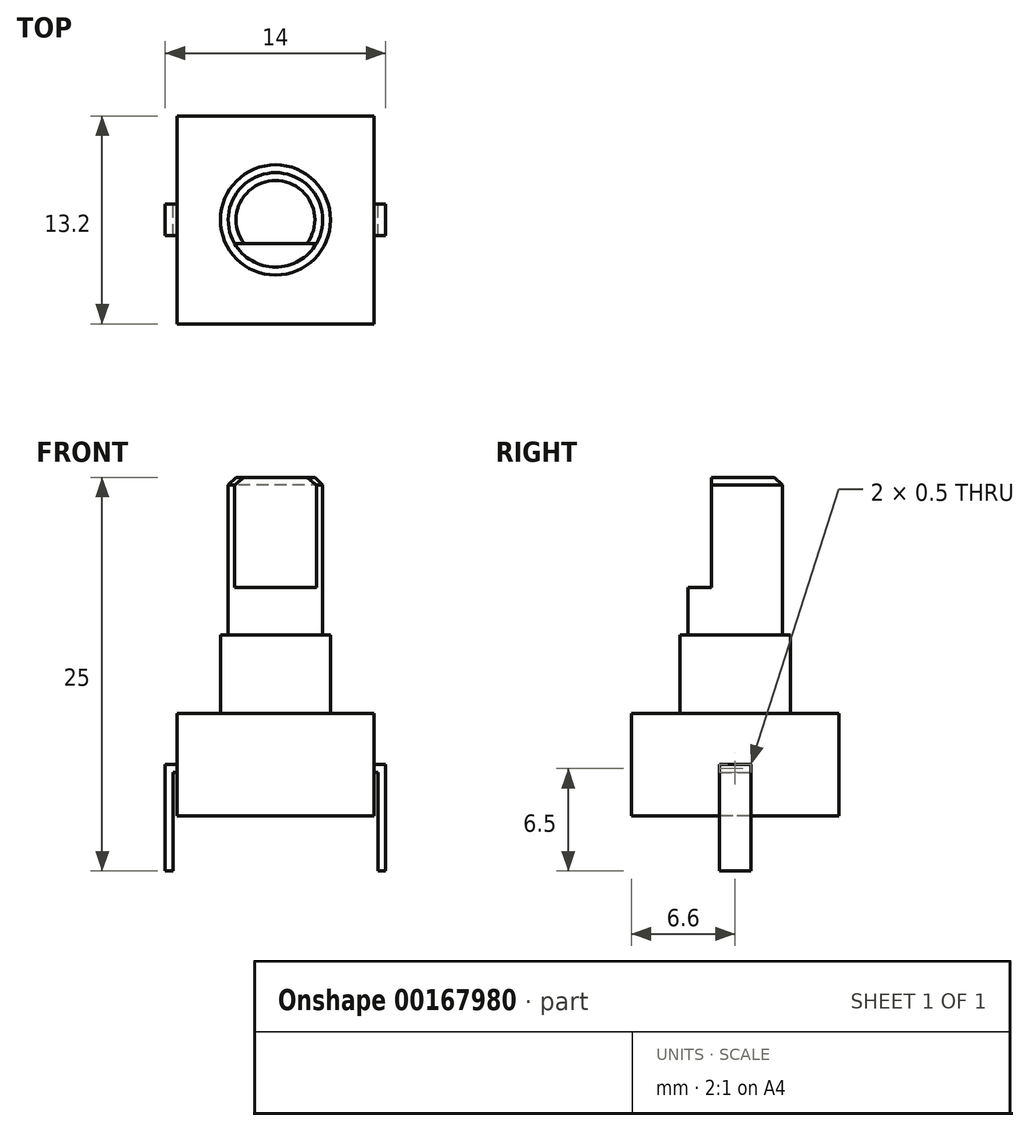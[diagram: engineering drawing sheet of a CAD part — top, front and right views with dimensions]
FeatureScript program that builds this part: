
annotation { "Feature Type Name" : "Feature", "Feature Type Description" : "" }
export const myFeature = defineFeature(function(context is Context, id is Id, definition is map)
    precondition{}
    {
        {
            var Q0;
            Q0=qCreatedBy(makeId("Top.planeOp"),FACE);
            var sketch = newSketch(context, id + "F0", { "sketchPlane" : qUnion([Q0])});
            skLineSegment(sketch, "E0.bottom", {"start": v(6.25, 6.6) * mm, "end": v(-6.25, 6.6) * mm});
            skLineSegment(sketch, "E0.top", {"start": v(6.25, -6.6) * mm, "end": v(-6.25, -6.6) * mm});
            skLineSegment(sketch, "E0.left", {"start": v(6.25, 6.6) * mm, "end": v(6.25, -6.6) * mm});
            skLineSegment(sketch, "E0.right", {"start": v(-6.25, 6.6) * mm, "end": v(-6.25, -6.6) * mm});
            skPoint(sketch, "E0.middle", {"position": v(0, 0) * mm});
            skSolve(sketch);
        }
        {
            var Q0;
            Q0 = qSketchRegion(id + "F0", true);
            extrude(context, id + "F1", {"entities" : qUnion([Q0]), "depth" : 6.5 * mm});
        }
        {
            var Q0;
            Q0=makeQuery(id+"F1.opExtrude","CAP_FACE",FACE,{"disambiguationData":[OSD([sQuery(id+"F0.wireOp",EDGE,"E0.bottom"),sQuery(id+"F0.wireOp",EDGE,"E0.top"),sQuery(id+"F0.wireOp",EDGE,"E0.left"),sQuery(id+"F0.wireOp",EDGE,"E0.right")])],"isStart":false});
            var sketch = newSketch(context, id + "F2", { "sketchPlane" : qUnion([Q0])});
            skCircle(sketch, "E1", {"center": v(0, 0) * mm, "radius": 3.5 * mm});
            skSolve(sketch);
        }
        {
            var Q0;
            Q0 = qSketchRegion(id + "F2", true);
            extrude(context, id + "F3", {"entities" : qUnion([Q0]), "operationType" : NewBodyOperationType.ADD, "depth" : 5 * mm});
        }
        {
            var Q0;
            Q0=makeQuery(id+"F3.opExtrude","CAP_FACE",FACE,{"disambiguationData":[OSD([sQuery(id+"F2.wireOp",EDGE,"E1")])],"isStart":false});
            var sketch = newSketch(context, id + "F4", { "sketchPlane" : qUnion([Q0])});
            skCircle(sketch, "E2", {"center": v(0, 0) * mm, "radius": 3 * mm});
            skSolve(sketch);
        }
        {
            var Q0;
            Q0 = qSketchRegion(id + "F4", true);
            extrude(context, id + "F5", {"entities" : qUnion([Q0]), "operationType" : NewBodyOperationType.ADD, "depth" : 10 * mm});
        }
        {
            var Q0;
            Q0=makeQuery(id+"F5.opExtrude","CAP_EDGE",EDGE,{"disambiguationData":[OSD([sQuery(id+"F4.wireOp",EDGE,"E2")])],"isStart":false});
            chamfer(context, id + "F6", {"entities" : qUnion([Q0]), "width" : 0.5 * mm, "tangentPropagation" : true});
        }
        {
            var Q0;
            Q0=makeQuery(id+"F5.opExtrude","CAP_FACE",FACE,{"disambiguationData":[OSD([sQuery(id+"F4.wireOp",EDGE,"E2")])],"isStart":false});
            var sketch = newSketch(context, id + "F7", { "sketchPlane" : qUnion([Q0])});
            skLineSegment(sketch, "E3", {"start": v(-13.83, -3) * mm, "end": v(13.83, -3) * mm, "construction": true});
            skLineSegment(sketch, "E4.bottom", {"start": v(-6.35, -3) * mm, "end": v(6.35, -3) * mm});
            skLineSegment(sketch, "E4.top", {"start": v(-6.35, -1.5) * mm, "end": v(6.35, -1.5) * mm});
            skLineSegment(sketch, "E4.left", {"start": v(-6.35, -3) * mm, "end": v(-6.35, -1.5) * mm});
            skLineSegment(sketch, "E4.right", {"start": v(6.35, -3) * mm, "end": v(6.35, -1.5) * mm});
            skPoint(sketch, "E5", {"position": v(0, -3) * mm});
            skSolve(sketch);
        }
        {
            var Q0;
            Q0 = qSketchRegion(id + "F7", true);
            extrude(context, id + "F8", {"entities" : qUnion([Q0]), "operationType" : NewBodyOperationType.REMOVE, "oppositeDirection" : true, "depth" : 7 * mm});
        }
        {
            var Q0;
            Q0=qCreatedBy(makeId("Front.planeOp"),FACE);
            var sketch = newSketch(context, id + "F9", { "sketchPlane" : qUnion([Q0])});
            skLineSegment(sketch, "E6", {"start": v(-7, 3.25) * mm, "end": v(-7, -3.5) * mm});
            skLineSegment(sketch, "E7", {"start": v(-7, -3.5) * mm, "end": v(-6.5, -3.5) * mm});
            skLineSegment(sketch, "E8", {"start": v(-6.5, -3.5) * mm, "end": v(-6.5, 2.75) * mm});
            skLineSegment(sketch, "E9", {"start": v(-6.5, 2.75) * mm, "end": v(-6.25, 2.75) * mm});
            skLineSegment(sketch, "E10", {"start": v(-7, 3.25) * mm, "end": v(-6.25, 3.25) * mm});
            skLineSegment(sketch, "E11.0", {"start": v(-6.25, 6.5) * mm, "end": v(-6.25, 0) * mm, "construction": true});
            skLineSegment(sketch, "E12", {"start": v(-6.25, 3.25) * mm, "end": v(-6.25, 2.75) * mm});
            skLineSegment(sketch, "E13.MirrorCS", {"start": v(6.5, 2.75) * mm, "end": v(6.25, 2.75) * mm});
            skLineSegment(sketch, "E14.MirrorCS", {"start": v(7, -3.5) * mm, "end": v(6.5, -3.5) * mm});
            skLineSegment(sketch, "E15.MirrorCS", {"start": v(7, 3.25) * mm, "end": v(7, -3.5) * mm});
            skLineSegment(sketch, "E16.MirrorCS", {"start": v(6.5, -3.5) * mm, "end": v(6.5, 2.75) * mm});
            skLineSegment(sketch, "E17.MirrorCS", {"start": v(7, 3.25) * mm, "end": v(6.25, 3.25) * mm});
            skLineSegment(sketch, "E18.MirrorCS", {"start": v(6.25, 3.25) * mm, "end": v(6.25, 2.75) * mm});
            skSolve(sketch);
        }
        {
            var Q0;
            Q0 = qSketchRegion(id + "F9", true);
            extrude(context, id + "F10", {"entities" : qUnion([Q0]), "operationType" : NewBodyOperationType.ADD, "endBound" : BoundingType.SYMMETRIC, "depth" : 2 * mm});
        }
    });
